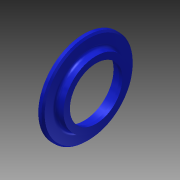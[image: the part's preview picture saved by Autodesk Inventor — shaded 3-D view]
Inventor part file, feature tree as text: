
AUTODESK INVENTOR PART (.ipt)
format: ipt  version: 2014 (Build 180170000, 170)  size: 144,384 bytes
history: native  units: in
note: dims shown in document units (in); Inventor stores cm internally (conversion verified against a paired STEP export)
features: reference x8, chamfer x2, sketch x2, revolve x1, plane x1, extrude x1
ambient origin geometry x8: Origin, YZ Plane, XZ Plane, XY Plane, X Axis, Y Axis, Z Axis, Center Point
bodies: Solid1 (feature_tree)
feature tree (15):
  revolve  "Revolution1"  [1 undecoded]
  chamfer  "Chamfer1"  Distance=0.01in
  plane  "Work Plane1"
  extrude  "Extrusion1"  Depth=0.1in
  chamfer  "Chamfer2"  Distance=0.1in
  sketch  "Sketch1"  dims[d0=0.025in d1=0.025in]
  reference  "Reference1"
  reference  "Reference2"
  reference  "Reference3"
  reference  "Reference4"
  reference  "Reference5"
  reference  "Reference6"
  reference  "Reference7"
  reference  "Reference8"
  sketch  "Sketch2"  dims[d2=0.3in d3=0.01in d4=0.01in d5=0.1in d6=0.1in d7=0.05in d9=0.5in d10=0.1001in d11=90.0deg d12=0.05in d13=0.125in d14=45.0deg d15=0.0in d16=0.0in d17=0.05in d18=0.125in d19=45.0deg]
note: 1 required parameter value undecoded (feature->parameter linkage not recoverable at this tier; creation-order binding heuristic only, values carry confidence <= 0.55)
